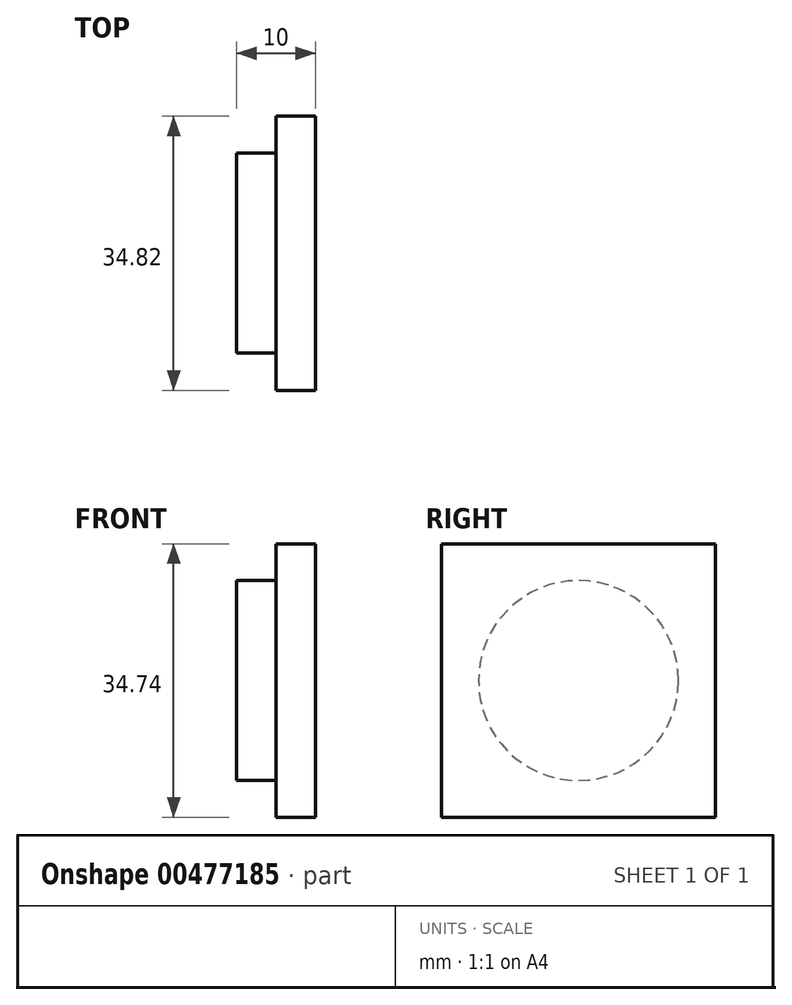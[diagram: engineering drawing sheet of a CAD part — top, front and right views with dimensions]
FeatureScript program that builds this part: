
annotation { "Feature Type Name" : "Feature", "Feature Type Description" : "" }
export const myFeature = defineFeature(function(context is Context, id is Id, definition is map)
    precondition{}
    {
        {
            var Q0;
            Q0=qCreatedBy(makeId("Right.planeOp"),FACE);
            var sketch = newSketch(context, id + "F0", { "sketchPlane" : qUnion([Q0])});
            skCircle(sketch, "E0", {"center": v(0, 0) * mm, "radius": 12.7 * mm});
            skSolve(sketch);
        }
        {
            var Q0;
            Q0 = qSketchRegion(id + "F0", true);
            extrude(context, id + "F1", {"entities" : qUnion([Q0]), "depth" : 5 * mm});
        }
        {
            var Q0;
            Q0=makeQuery(id+"F1.opExtrude","CAP_FACE",FACE,{"disambiguationData":[OSD([sQuery(id+"F0.wireOp",EDGE,"E0")])],"isStart":false});
            var sketch = newSketch(context, id + "F2", { "sketchPlane" : qUnion([Q0])});
            skLineSegment(sketch, "E1.bottom", {"start": v(17.4, -17.37) * mm, "end": v(-17.4, -17.37) * mm});
            skLineSegment(sketch, "E1.top", {"start": v(17.4, 17.37) * mm, "end": v(-17.4, 17.37) * mm});
            skLineSegment(sketch, "E1.left", {"start": v(17.4, -17.37) * mm, "end": v(17.4, 17.37) * mm});
            skLineSegment(sketch, "E1.right", {"start": v(-17.4, -17.37) * mm, "end": v(-17.4, 17.37) * mm});
            skPoint(sketch, "E1.middle", {"position": v(0, 0) * mm});
            skSolve(sketch);
        }
        {
            var Q0;
            Q0 = qSketchRegion(id + "F2", true);
            extrude(context, id + "F3", {"entities" : qUnion([Q0]), "operationType" : NewBodyOperationType.ADD, "depth" : 5 * mm});
        }
    });
